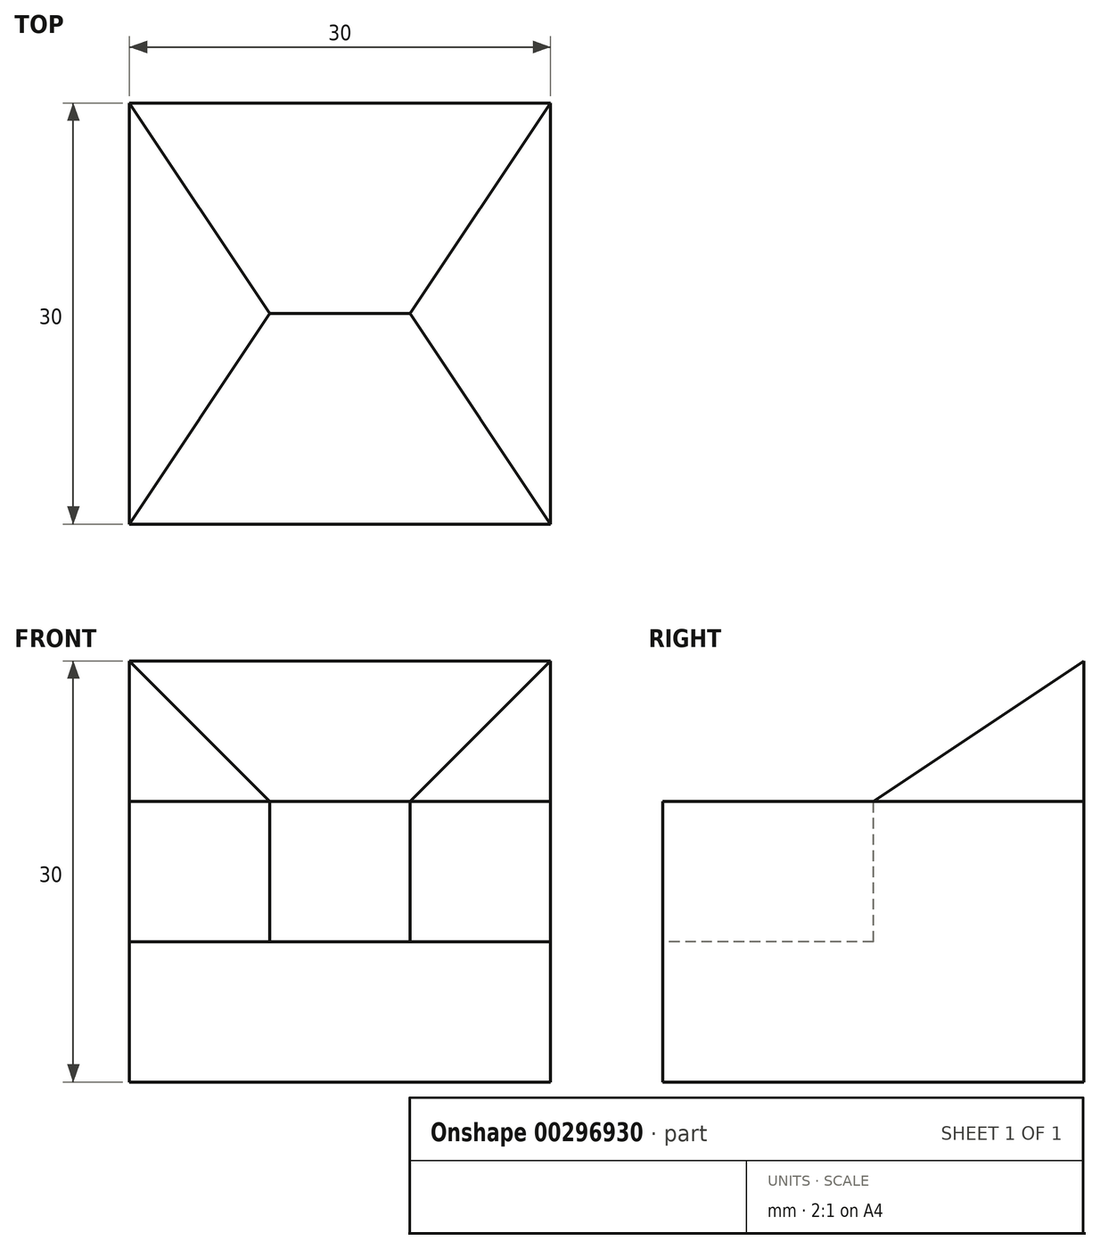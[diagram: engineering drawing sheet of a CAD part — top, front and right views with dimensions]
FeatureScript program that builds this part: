
annotation { "Feature Type Name" : "Feature", "Feature Type Description" : "" }
export const myFeature = defineFeature(function(context is Context, id is Id, definition is map)
    precondition{}
    {
        {
            var Q0;
            Q0=qCreatedBy(makeId("Top.planeOp"),FACE);
            var sketch = newSketch(context, id + "F0", { "sketchPlane" : qUnion([Q0])});
            skLineSegment(sketch, "E0.bottom", {"start": v(0, 0) * mm, "end": v(30, 0) * mm});
            skLineSegment(sketch, "E0.top", {"start": v(0, 30) * mm, "end": v(30, 30) * mm});
            skLineSegment(sketch, "E0.left", {"start": v(0, 0) * mm, "end": v(0, 30) * mm});
            skLineSegment(sketch, "E0.right", {"start": v(30, 0) * mm, "end": v(30, 30) * mm});
            skLineSegment(sketch, "E1", {"start": v(0, 30) * mm, "end": v(10, 15) * mm});
            skLineSegment(sketch, "E2", {"start": v(10, 15) * mm, "end": v(0, 0) * mm});
            skLineSegment(sketch, "E3", {"start": v(10, 15) * mm, "end": v(20, 15) * mm});
            skLineSegment(sketch, "E4", {"start": v(20, 15) * mm, "end": v(30, 30) * mm});
            skLineSegment(sketch, "E5", {"start": v(20, 15) * mm, "end": v(30, 0) * mm});
            skSolve(sketch);
        }
        {
            var Q0;
            Q0=qSketchRegion(id+"F0",true);
            extrude(context, id + "F1", {"entities" : qUnion([Q0]), "oppositeDirection" : true, "depth" : 30 * mm});
        }
        {
            var Q0;
            Q0=makeQuery(id+"F0.imprint","IMPRINT",FACE,{"disambiguationData":[TD([[makeQuery(id+"F0.imprint","IMPRINT",EDGE,{"derivedFrom":sQuery(id+"F0.wireOp",EDGE,"E0.bottom")}),1.0]])]});
            extrude(context, id + "F2", {"entities" : qUnion([Q0]), "operationType" : NewBodyOperationType.REMOVE, "oppositeDirection" : true, "depth" : 20 * mm});
        }
        {
            var Q0;
            Q0=makeQuery(id+"F0.imprint","IMPRINT",FACE,{"disambiguationData":[TD([[makeQuery(id+"F0.imprint","IMPRINT",EDGE,{"derivedFrom":sQuery(id+"F0.wireOp",EDGE,"E0.left")}),-1.0]])]});
            var Q1;
            Q1=makeQuery(id+"F0.imprint","IMPRINT",FACE,{"disambiguationData":[TD([[makeQuery(id+"F0.imprint","IMPRINT",EDGE,{"derivedFrom":sQuery(id+"F0.wireOp",EDGE,"E0.right")}),1.0]])]});
            extrude(context, id + "F3", {"entities" : qUnion([Q0, Q1]), "operationType" : NewBodyOperationType.REMOVE, "oppositeDirection" : true, "depth" : 10 * mm});
        }
        {
            var Q0;
            Q0=makeQuery(id+"F1.opExtrude","SWEPT_FACE",FACE,{"disambiguationData":[OSD([sQuery(id+"F0.wireOp",EDGE,"E0.right")])]});
            var sketch = newSketch(context, id + "F4", { "sketchPlane" : qUnion([Q0])});
            skLineSegment(sketch, "E6.0", {"start": v(15, 0) * mm, "end": v(30, 0) * mm});
            skLineSegment(sketch, "E7", {"start": v(15, -10) * mm, "end": v(30, 0) * mm});
            skLineSegment(sketch, "E8", {"start": v(15, 0) * mm, "end": v(15, -10) * mm});
            skSolve(sketch);
        }
        {
            var Q0;
            Q0=makeQuery(id+"F4.imprint","IMPRINT",FACE,{"disambiguationData":[TD([[makeQuery(id+"F4.imprint","IMPRINT",EDGE,{"derivedFrom":sQuery(id+"F4.wireOp",EDGE,"E6.0")}),-1.0]])]});
            extrude(context, id + "F5", {"entities" : qUnion([Q0]), "operationType" : NewBodyOperationType.REMOVE, "endBound" : BoundingType.THROUGH_ALL, "oppositeDirection" : true, "depth" : 25 * mm});
        }
    });
